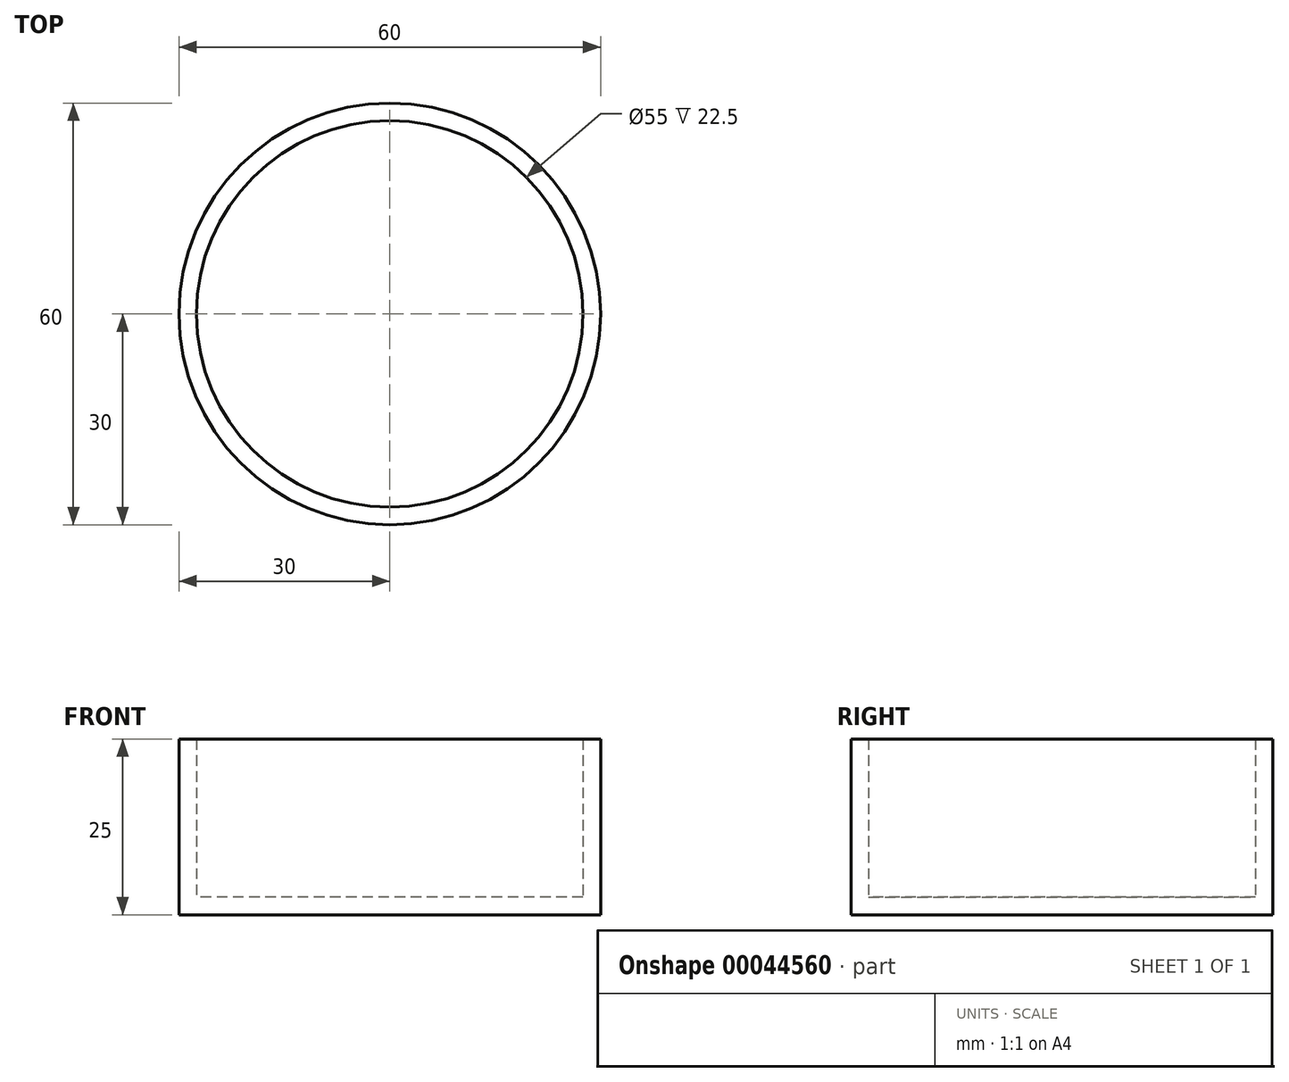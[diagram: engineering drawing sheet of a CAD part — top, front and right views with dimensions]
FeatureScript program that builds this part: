
annotation { "Feature Type Name" : "Feature", "Feature Type Description" : "" }
export const myFeature = defineFeature(function(context is Context, id is Id, definition is map)
    precondition{}
    {
        {
            var Q0;
            Q0=qCreatedBy(makeId("Top.planeOp"),FACE);
            var sketch = newSketch(context, id + "F0", { "sketchPlane" : qUnion([Q0])});
            skLineSegment(sketch, "E0.rect.bottom", {"start": v(100, -75) * mm, "end": v(-100, -75) * mm});
            skLineSegment(sketch, "E0.rect.top", {"start": v(100, 75) * mm, "end": v(-100, 75) * mm});
            skLineSegment(sketch, "E0.rect.left", {"start": v(100, -75) * mm, "end": v(100, 75) * mm});
            skLineSegment(sketch, "E0.rect.right", {"start": v(-100, -75) * mm, "end": v(-100, 75) * mm});
            skPoint(sketch, "E0.rect.middle", {"position": v(0, 0) * mm});
            skSolve(sketch);
        }
        {
            var Q0;
            Q0=qSketchRegion(id+"F0",true);
            extrude(context, id + "F1", {"entities" : qUnion([Q0]), "depth" : 100 * mm});
        }
        {
            var Q0;
            Q0=makeQuery(id+"F1.opExtrude","CAP_FACE",FACE,{"disambiguationData":[OSD([sQuery(id+"F0.wireOp",EDGE,"E0.rect.bottom"),sQuery(id+"F0.wireOp",EDGE,"E0.rect.top"),sQuery(id+"F0.wireOp",EDGE,"E0.rect.left"),sQuery(id+"F0.wireOp",EDGE,"E0.rect.right")])],"isStart":false});
            shell(context, id + "F2", {"entities" : qUnion([Q0]), "thickness" : 2.5 * mm});
        }
        {
            var Q0;
            Q0=makeQuery(id+"F1.opExtrude","SWEPT_EDGE",EDGE,{"disambiguationData":[OSD([sQuery(id+"F0.wireOp",EDGE,"E0.rect.bottom"),sQuery(id+"F0.wireOp",EDGE,"E0.rect.right")])]});
            var Q1;
            Q1=makeQuery(id+"F1.opExtrude","SWEPT_EDGE",EDGE,{"disambiguationData":[OSD([sQuery(id+"F0.wireOp",EDGE,"E0.rect.top"),sQuery(id+"F0.wireOp",EDGE,"E0.rect.right")])]});
            var Q2;
            Q2=makeQuery(id+"F1.opExtrude","SWEPT_EDGE",EDGE,{"disambiguationData":[OSD([sQuery(id+"F0.wireOp",EDGE,"E0.rect.top"),sQuery(id+"F0.wireOp",EDGE,"E0.rect.left")])]});
            var Q3;
            Q3=makeQuery(id+"F1.opExtrude","SWEPT_EDGE",EDGE,{"disambiguationData":[OSD([sQuery(id+"F0.wireOp",EDGE,"E0.rect.bottom"),sQuery(id+"F0.wireOp",EDGE,"E0.rect.left")])]});
            fillet(context, id + "F3", {"entities" : qUnion([Q0, Q1, Q2, Q3]), "radius" : 5 * mm, "tangentPropagation" : true, "allowEdgeOverflow" : false});
        }
        {
            var Q0;
            Q0=makeQuery(id+"F1.opExtrude","SWEPT_BODY",BODY,{"disambiguationData":[OSD([sQuery(id+"F0.wireOp",EDGE,"E0.rect.bottom"),sQuery(id+"F0.wireOp",EDGE,"E0.rect.top"),sQuery(id+"F0.wireOp",EDGE,"E0.rect.left"),sQuery(id+"F0.wireOp",EDGE,"E0.rect.right")])]});
            deleteBodies(context, id + "F4", {"entities" : qUnion([Q0])});
        }
        {
            var Q0;
            Q0=qCreatedBy(makeId("Top.planeOp"),FACE);
            var sketch = newSketch(context, id + "F5", { "sketchPlane" : qUnion([Q0])});
            skCircle(sketch, "E1", {"center": v(0, 0) * mm, "radius": 30 * mm});
            skSolve(sketch);
        }
        {
            var Q0;
            Q0=makeQuery(id+"F5.imprint","IMPRINT",FACE,{"disambiguationData":[TD([[makeQuery(id+"F5.imprint","IMPRINT",EDGE,{"derivedFrom":sQuery(id+"F5.wireOp",EDGE,"E1")}),1.0]])]});
            extrude(context, id + "F6", {"entities" : qUnion([Q0]), "depth" : 25 * mm});
        }
        {
            var Q0;
            Q0=makeQuery(id+"F6.opExtrude","CAP_FACE",FACE,{"disambiguationData":[OSD([sQuery(id+"F5.wireOp",EDGE,"E1")])],"isStart":false});
            shell(context, id + "F7", {"entities" : qUnion([Q0]), "thickness" : 2.5 * mm});
        }
    });
